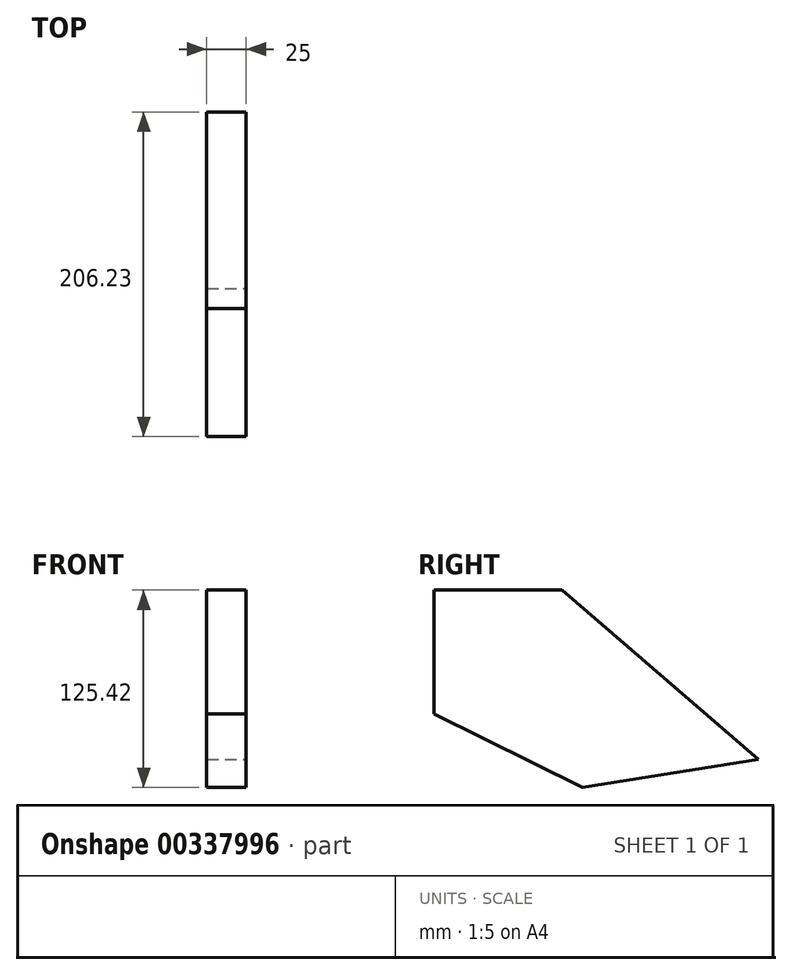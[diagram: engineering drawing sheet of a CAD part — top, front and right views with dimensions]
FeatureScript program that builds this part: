
annotation { "Feature Type Name" : "Feature", "Feature Type Description" : "" }
export const myFeature = defineFeature(function(context is Context, id is Id, definition is map)
    precondition{}
    {
        {
            var Q0;
            Q0=qCreatedBy(makeId("Right.planeOp"),FACE);
            var sketch = newSketch(context, id + "F0", { "sketchPlane" : qUnion([Q0])});
            skLineSegment(sketch, "E0.bottom", {"start": v(-58.25, 49.84) * mm, "end": v(23.11, 49.84) * mm});
            skLineSegment(sketch, "E0.top", {"start": v(-58.25, -28.78) * mm, "end": v(23.11, -28.78) * mm});
            skLineSegment(sketch, "E0.left", {"start": v(-58.25, 49.84) * mm, "end": v(-58.25, -28.78) * mm});
            skLineSegment(sketch, "E0.right", {"start": v(23.11, 49.84) * mm, "end": v(23.11, -28.78) * mm});
            skLineSegment(sketch, "E1", {"start": v(23.11, 49.84) * mm, "end": v(147.98, -57.68) * mm});
            skLineSegment(sketch, "E2", {"start": v(147.98, -57.68) * mm, "end": v(23.11, -28.78) * mm});
            skLineSegment(sketch, "E3", {"start": v(147.98, -57.68) * mm, "end": v(35.98, -75.58) * mm});
            skLineSegment(sketch, "E4", {"start": v(-58.25, -28.78) * mm, "end": v(35.98, -75.58) * mm});
            skSolve(sketch);
        }
        {
            var Q0;
            Q0=makeQuery(id+"F0.imprint","IMPRINT",FACE,{"disambiguationData":[TD([[makeQuery(id+"F0.imprint","IMPRINT",EDGE,{"derivedFrom":sQuery(id+"F0.wireOp",EDGE,"E0.top")}),-1.0]])]});
            var Q1;
            Q1=makeQuery(id+"F0.imprint","IMPRINT",FACE,{"disambiguationData":[TD([[makeQuery(id+"F0.imprint","IMPRINT",EDGE,{"derivedFrom":sQuery(id+"F0.wireOp",EDGE,"E0.right")}),1.0]])]});
            var Q2;
            Q2=makeQuery(id+"F0.imprint","IMPRINT",FACE,{"disambiguationData":[TD([[makeQuery(id+"F0.imprint","IMPRINT",EDGE,{"derivedFrom":sQuery(id+"F0.wireOp",EDGE,"E0.bottom")}),-1.0]])]});
            extrude(context, id + "F1", {"entities" : qUnion([Q0, Q1, Q2]), "oppositeDirection" : true, "depth" : 25 * mm});
        }
    });
